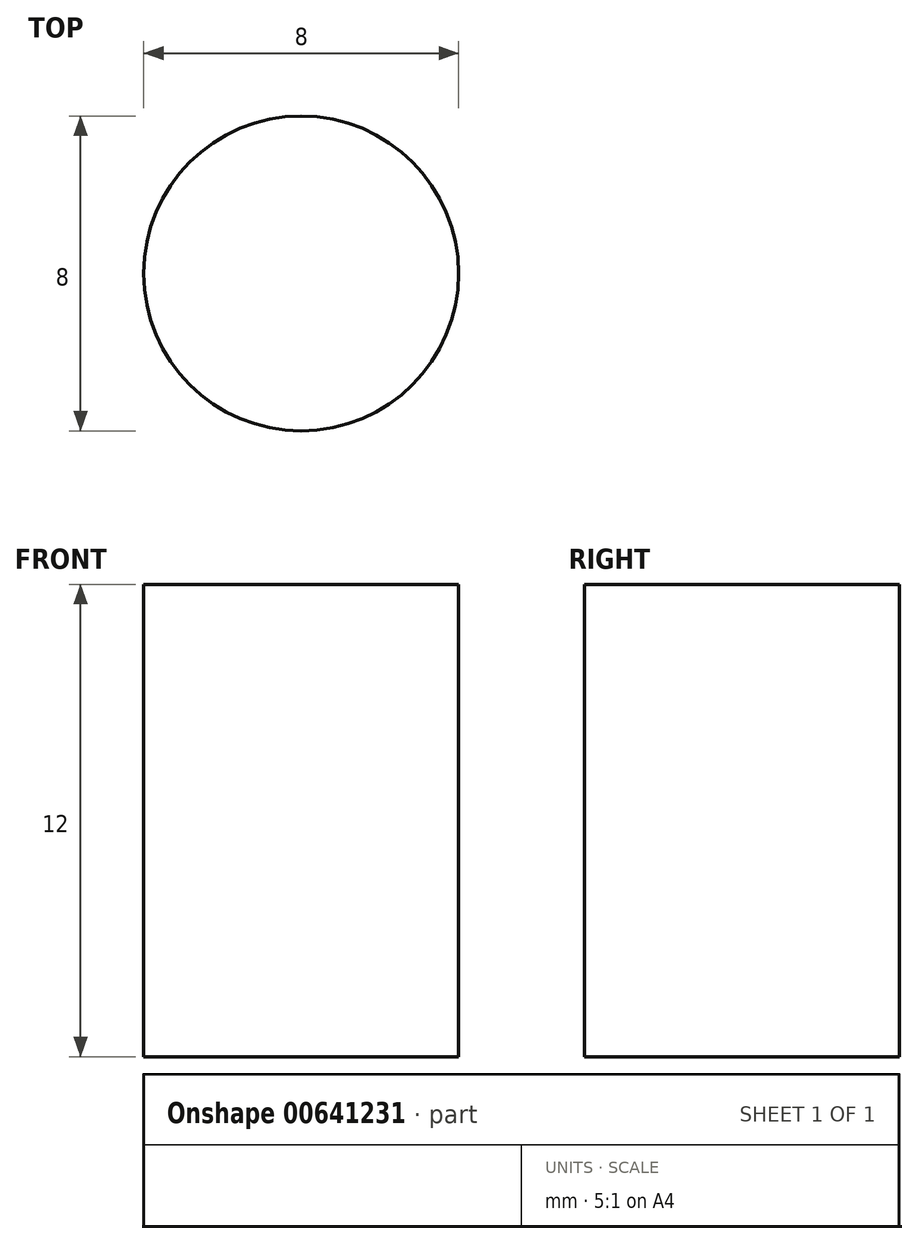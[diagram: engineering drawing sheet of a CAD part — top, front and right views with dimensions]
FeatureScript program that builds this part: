
annotation { "Feature Type Name" : "Feature", "Feature Type Description" : "" }
export const myFeature = defineFeature(function(context is Context, id is Id, definition is map)
    precondition{}
    {
        {
            var Q0;
            Q0=qCreatedBy(makeId("Top.planeOp"),FACE);
            var sketch = newSketch(context, id + "F0", { "sketchPlane" : qUnion([Q0])});
            skCircle(sketch, "E0", {"center": v(0, 0) * mm, "radius": 45 * mm, "construction": true});
            skCircle(sketch, "E1", {"center": v(0, 0) * mm, "radius": 42 * mm, "construction": true});
            skCircle(sketch, "E2", {"center": v(80, -30) * mm, "radius": 8 * mm, "construction": true});
            skCircle(sketch, "E3", {"center": v(72, 32) * mm, "radius": 4 * mm});
            skArc(sketch, "E4", {"start": v(-41.8, 4.01) * mm, "mid": v(-32.17, -27) * mm, "end": v(-3.3, -41.87) * mm});
            skArc(sketch, "E5", {"start": v(24.38, 34.2) * mm, "mid": v(-7.3, 41.36) * mm, "end": v(-34.6, 23.8) * mm});
            skArc(sketch, "E6", {"start": v(80.4, -37.99) * mm, "mid": v(87.73, -32.05) * mm, "end": v(84.31, -23.26) * mm});
            skArc(sketch, "E7", {"start": v(79, -8) * mm, "mid": v(77.59, -8.59) * mm, "end": v(77, -10) * mm});
            skCircle(sketch, "E8", {"center": v(80, -30) * mm, "radius": 4 * mm});
            skArc(sketch, "E9", {"start": v(77, -15.58) * mm, "mid": v(77.67, -18.21) * mm, "end": v(79.53, -20.2) * mm});
            skLineSegment(sketch, "E10", {"start": v(50, 0) * mm, "end": v(100, 0) * mm, "construction": true});
            skLineSegment(sketch, "E11", {"start": v(101, 23) * mm, "end": v(57.1, 23) * mm, "construction": true});
            skLineSegment(sketch, "E12", {"start": v(84, 34) * mm, "end": v(84, -19) * mm, "construction": true});
            skLineSegment(sketch, "E13", {"start": v(23.58, 25.52) * mm, "end": v(94.36, 25.52) * mm, "construction": true});
            skLineSegment(sketch, "E14", {"start": v(70, -19.5) * mm, "end": v(70, 34) * mm, "construction": true});
            skLineSegment(sketch, "E15", {"start": v(45.81, 25.52) * mm, "end": v(51.61, 25.52) * mm});
            skLineSegment(sketch, "E16", {"start": v(79.53, -20.2) * mm, "end": v(84.31, -23.26) * mm});
            skLineSegment(sketch, "E17", {"start": v(77, -10) * mm, "end": v(77, -15.58) * mm});
            skCircle(sketch, "E18", {"center": v(0, 0) * mm, "radius": 26 * mm, "construction": true});
            skLineSegment(sketch, "E19", {"start": v(-58.5, 0) * mm, "end": v(-86.23, 0) * mm, "construction": true});
            skLineSegment(sketch, "E20", {"start": v(0, 0) * mm, "end": v(-64.52, 23.48) * mm, "construction": true});
            skLineSegment(sketch, "E21", {"start": v(0, 0) * mm, "end": v(51.73, 43.4) * mm, "construction": true});
            skLineSegment(sketch, "E22", {"start": v(0, 0) * mm, "end": v(11.18, -63.43) * mm, "construction": true});
            skCircle(sketch, "E23", {"center": v(-42.29, 15.4) * mm, "radius": 4 * mm});
            skCircle(sketch, "E24", {"center": v(34.47, 28.93) * mm, "radius": 4 * mm});
            skCircle(sketch, "E25", {"center": v(7.81, -44.32) * mm, "radius": 4 * mm});
            skArc(sketch, "E26", {"start": v(-38.9, 22.64) * mm, "mid": v(-49.8, 18.13) * mm, "end": v(-44.34, 7.66) * mm});
            skArc(sketch, "E27", {"start": v(42.47, 28.88) * mm, "mid": v(37.55, 36.31) * mm, "end": v(28.8, 34.57) * mm});
            skArc(sketch, "E28", {"start": v(-38.9, 22.64) * mm, "mid": v(-36.54, 22.43) * mm, "end": v(-34.6, 23.8) * mm});
            skArc(sketch, "E29", {"start": v(-41.8, 4.01) * mm, "mid": v(-42.4, 6.3) * mm, "end": v(-44.34, 7.66) * mm});
            skArc(sketch, "E30", {"start": v(24.38, 34.2) * mm, "mid": v(26.66, 33.57) * mm, "end": v(28.8, 34.57) * mm});
            skArc(sketch, "E31", {"start": v(-0.16, -45) * mm, "mid": v(6.7, -52.24) * mm, "end": v(15.29, -47.17) * mm});
            skArc(sketch, "E32", {"start": v(-0.16, -45) * mm, "mid": v(-1.16, -42.86) * mm, "end": v(-3.3, -41.87) * mm});
            skLineSegment(sketch, "E33", {"start": v(80.4, -37.99) * mm, "end": v(24.01, -40.84) * mm});
            skArc(sketch, "E34", {"start": v(24.01, -40.84) * mm, "mid": v(18.7, -42.71) * mm, "end": v(15.29, -47.17) * mm});
            skArc(sketch, "E35", {"start": v(78.11, 26.43) * mm, "mid": v(77.73, 37.96) * mm, "end": v(66.2, 37.89) * mm});
            skArc(sketch, "E36", {"start": v(78.11, 26.43) * mm, "mid": v(77.75, 24.22) * mm, "end": v(79.63, 23) * mm});
            skLineSegment(sketch, "E37", {"start": v(55.1, 26.95) * mm, "end": v(66.2, 37.89) * mm});
            skArc(sketch, "E38", {"start": v(51.61, 25.52) * mm, "mid": v(53.5, 25.89) * mm, "end": v(55.1, 26.95) * mm});
            skArc(sketch, "E39", {"start": v(42.47, 28.88) * mm, "mid": v(43.44, 26.5) * mm, "end": v(45.81, 25.52) * mm});
            skLineSegment(sketch, "E40", {"start": v(30.4, -52.32) * mm, "end": v(59.36, -52.32) * mm, "construction": true});
            skPoint(sketch, "E40.startSnap0", {"position": v(6.7, -52.24) * mm});
            skLineSegment(sketch, "E41", {"start": v(53.76, 40.27) * mm, "end": v(72.7, 40.27) * mm, "construction": true});
            skLineSegment(sketch, "E42", {"start": v(84, -8.06) * mm, "end": v(84, 23) * mm});
            skLineSegment(sketch, "E43", {"start": v(79, -8) * mm, "end": v(84, -8.06) * mm});
            skLineSegment(sketch, "E44", {"start": v(79.63, 23) * mm, "end": v(84, 23) * mm});
            skCircle(sketch, "E45", {"center": v(0, 0) * mm, "radius": 34 * mm, "construction": true});
            skSolve(sketch);
        }
        {
            var Q0;
            Q0=qCreatedBy(makeId("Top.planeOp"),FACE);
            cPlane(context, id + "F1", {"entities" : qUnion([Q0]), "cplaneType" : CPlaneType.OFFSET, "offset" : 12 * mm, "width" : 150 * mm, "height" : 150 * mm});
        }
        {
            var Q0;
            Q0=qCreatedBy(makeId("Top.planeOp"),FACE);
            var sketch = newSketch(context, id + "F2", { "sketchPlane" : qUnion([Q0])});
            skCircle(sketch, "E46", {"center": v(0, 0) * mm, "radius": 26 * mm, "construction": true});
            skCircle(sketch, "E47", {"center": v(50, -8) * mm, "radius": 20 * mm, "construction": true});
            skLineSegment(sketch, "E48", {"start": v(-1.04, -25.98) * mm, "end": v(49.2, -27.98) * mm});
            skArc(sketch, "E49", {"start": v(14.14, 21.82) * mm, "mid": v(-24.78, 7.87) * mm, "end": v(-1.04, -25.98) * mm});
            skArc(sketch, "E50", {"start": v(49.2, -27.98) * mm, "mid": v(70, -8.31) * mm, "end": v(49.83, 12) * mm});
            skLineSegment(sketch, "E51", {"start": v(80.11, -30.33) * mm, "end": v(80.11, 1.67) * mm, "construction": true});
            skLineSegment(sketch, "E52", {"start": v(80.11, 1.67) * mm, "end": v(64.11, 1.67) * mm, "construction": true});
            skCircle(sketch, "E53", {"center": v(34.52, 28.87) * mm, "radius": 17 * mm, "construction": true});
            skLineSegment(sketch, "E54", {"start": v(14.14, 21.82) * mm, "end": v(25.27, 14.6) * mm});
            skLineSegment(sketch, "E55", {"start": v(49.83, 12) * mm, "end": v(34.66, 11.87) * mm});
            skArc(sketch, "E56", {"start": v(25.27, 14.6) * mm, "mid": v(29.77, 12.55) * mm, "end": v(34.66, 11.87) * mm});
            skSolve(sketch);
        }
        {
            var Q0;
            Q0=qCreatedBy(id+"F1.planeOp",FACE);
            var sketch = newSketch(context, id + "F3", { "sketchPlane" : qUnion([Q0])});
            skCircle(sketch, "E57", {"center": v(0, 0) * mm, "radius": 30 * mm, "construction": true});
            skCircle(sketch, "E58", {"center": v(50, -8) * mm, "radius": 20 * mm, "construction": true});
            skLineSegment(sketch, "E59", {"start": v(1.2, -29.98) * mm, "end": v(50.8, -27.98) * mm});
            skArc(sketch, "E60", {"start": v(18.33, 23.75) * mm, "mid": v(-28.58, 9.11) * mm, "end": v(1.2, -29.98) * mm});
            skArc(sketch, "E61", {"start": v(50.8, -27.98) * mm, "mid": v(69.96, -9.2) * mm, "end": v(53.2, 11.74) * mm});
            skCircle(sketch, "E62", {"center": v(34.5, 28.95) * mm, "radius": 14 * mm, "construction": true});
            skLineSegment(sketch, "E63", {"start": v(18.33, 23.75) * mm, "end": v(25.95, 17.87) * mm});
            skLineSegment(sketch, "E64", {"start": v(53.2, 11.74) * mm, "end": v(32.26, 15.13) * mm});
            skArc(sketch, "E65", {"start": v(25.95, 17.87) * mm, "mid": v(28.93, 16.1) * mm, "end": v(32.26, 15.13) * mm});
            skSolve(sketch);
        }
        {
            var Q0;
            Q0=makeQuery(id+"F0.imprint","IMPRINT",FACE,{"disambiguationData":[TD([[makeQuery(id+"F0.imprint","IMPRINT",EDGE,{"derivedFrom":sQuery(id+"F0.wireOp",EDGE,"E3")}),1.0]])]});
            extrude(context, id + "F4", {"entities" : qUnion([Q0]), "depth" : 12 * mm, "offsetDistance" : 25 * mm});
        }
        {
            var Q1;
            Q1 = qSketchRegion(id + "F3", true);
            var Q2;
            Q2 = qSketchRegion(id + "F2", true);
            loft(context, id + "F5", {"operationType" : NewBodyOperationType.REMOVE, "sheetProfilesArray" : [{ "sheetProfileEntities" : qUnion([Q1]) }, { "sheetProfileEntities" : qUnion([Q2]) }]});
        }
    });
